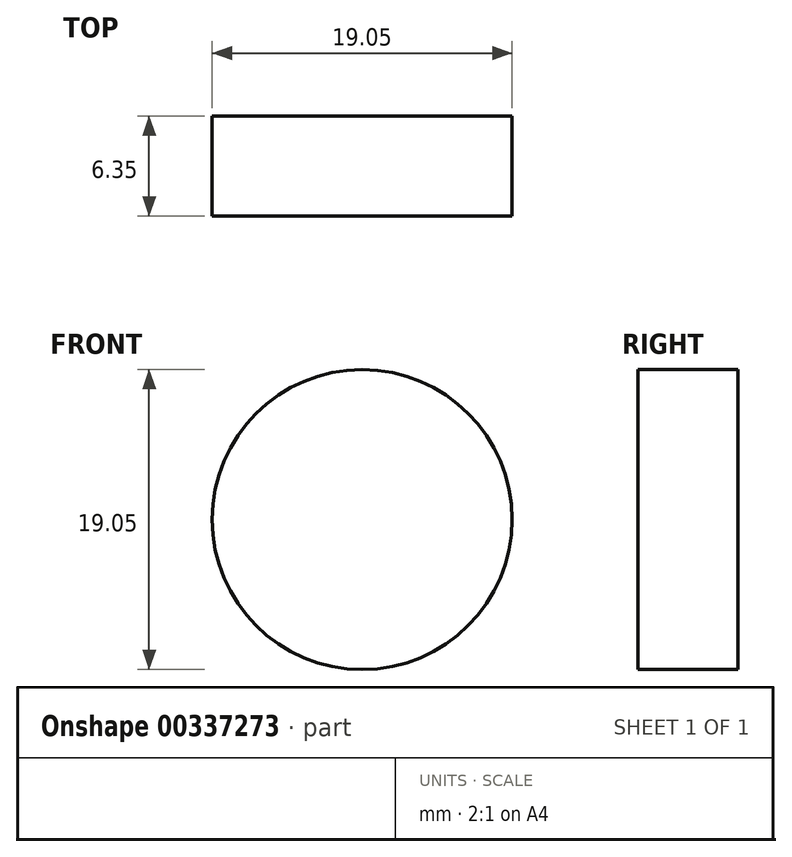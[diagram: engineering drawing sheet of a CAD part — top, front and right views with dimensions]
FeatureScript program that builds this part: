
annotation { "Feature Type Name" : "Feature", "Feature Type Description" : "" }
export const myFeature = defineFeature(function(context is Context, id is Id, definition is map)
    precondition{}
    {
        {
            var Q0;
            Q0=qCreatedBy(makeId("Front.planeOp"),FACE);
            var sketch = newSketch(context, id + "F0", { "sketchPlane" : qUnion([Q0])});
            skCircle(sketch, "E0", {"center": v(-63.6, 36.5) * mm, "radius": 9.53 * mm});
            skSolve(sketch);
        }
        {
            var Q0;
            Q0 = qSketchRegion(id + "F0", true);
            extrude(context, id + "F1", {"entities" : qUnion([Q0]), "depth" : 6.35 * mm});
        }
    });
